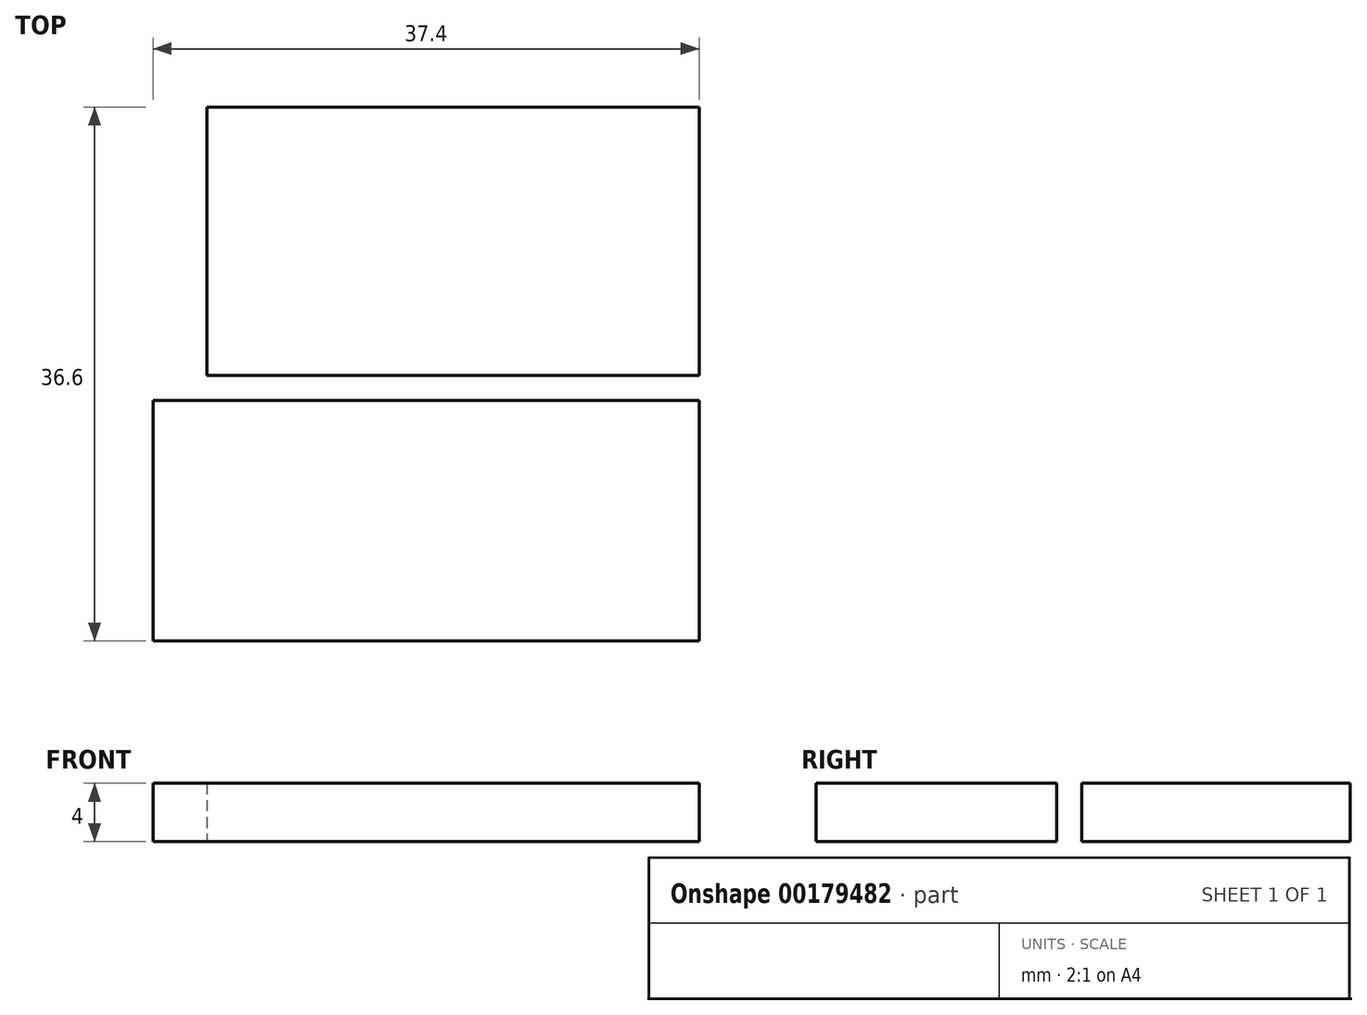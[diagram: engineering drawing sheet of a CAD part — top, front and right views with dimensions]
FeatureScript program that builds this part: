
annotation { "Feature Type Name" : "Feature", "Feature Type Description" : "" }
export const myFeature = defineFeature(function(context is Context, id is Id, definition is map)
    precondition{}
    {
        {
            var Q0;
            Q0=qCreatedBy(makeId("Top.planeOp"),FACE);
            var sketch = newSketch(context, id + "F0", { "sketchPlane" : qUnion([Q0])});
            skLineSegment(sketch, "E0.bottom", {"start": v(16.85, 9.2) * mm, "end": v(-16.85, 9.2) * mm});
            skLineSegment(sketch, "E0.top", {"start": v(16.85, -9.2) * mm, "end": v(-16.85, -9.2) * mm});
            skLineSegment(sketch, "E0.left", {"start": v(16.85, 9.2) * mm, "end": v(16.85, -9.2) * mm});
            skLineSegment(sketch, "E0.right", {"start": v(-16.85, 9.2) * mm, "end": v(-16.85, -9.2) * mm});
            skPoint(sketch, "E0.middle", {"position": v(0, 0) * mm});
            skLineSegment(sketch, "E1.bottom", {"start": v(16.85, -10.9) * mm, "end": v(-20.55, -10.9) * mm});
            skLineSegment(sketch, "E1.top", {"start": v(16.85, -27.4) * mm, "end": v(-20.55, -27.4) * mm});
            skLineSegment(sketch, "E1.left", {"start": v(16.85, -10.9) * mm, "end": v(16.85, -27.4) * mm});
            skLineSegment(sketch, "E1.right", {"start": v(-20.55, -10.9) * mm, "end": v(-20.55, -27.4) * mm});
            skSolve(sketch);
        }
        {
            var Q0;
            Q0 = qSketchRegion(id + "F0", true);
            extrude(context, id + "F1", {"entities" : qUnion([Q0]), "depth" : 4 * mm});
        }
    });
